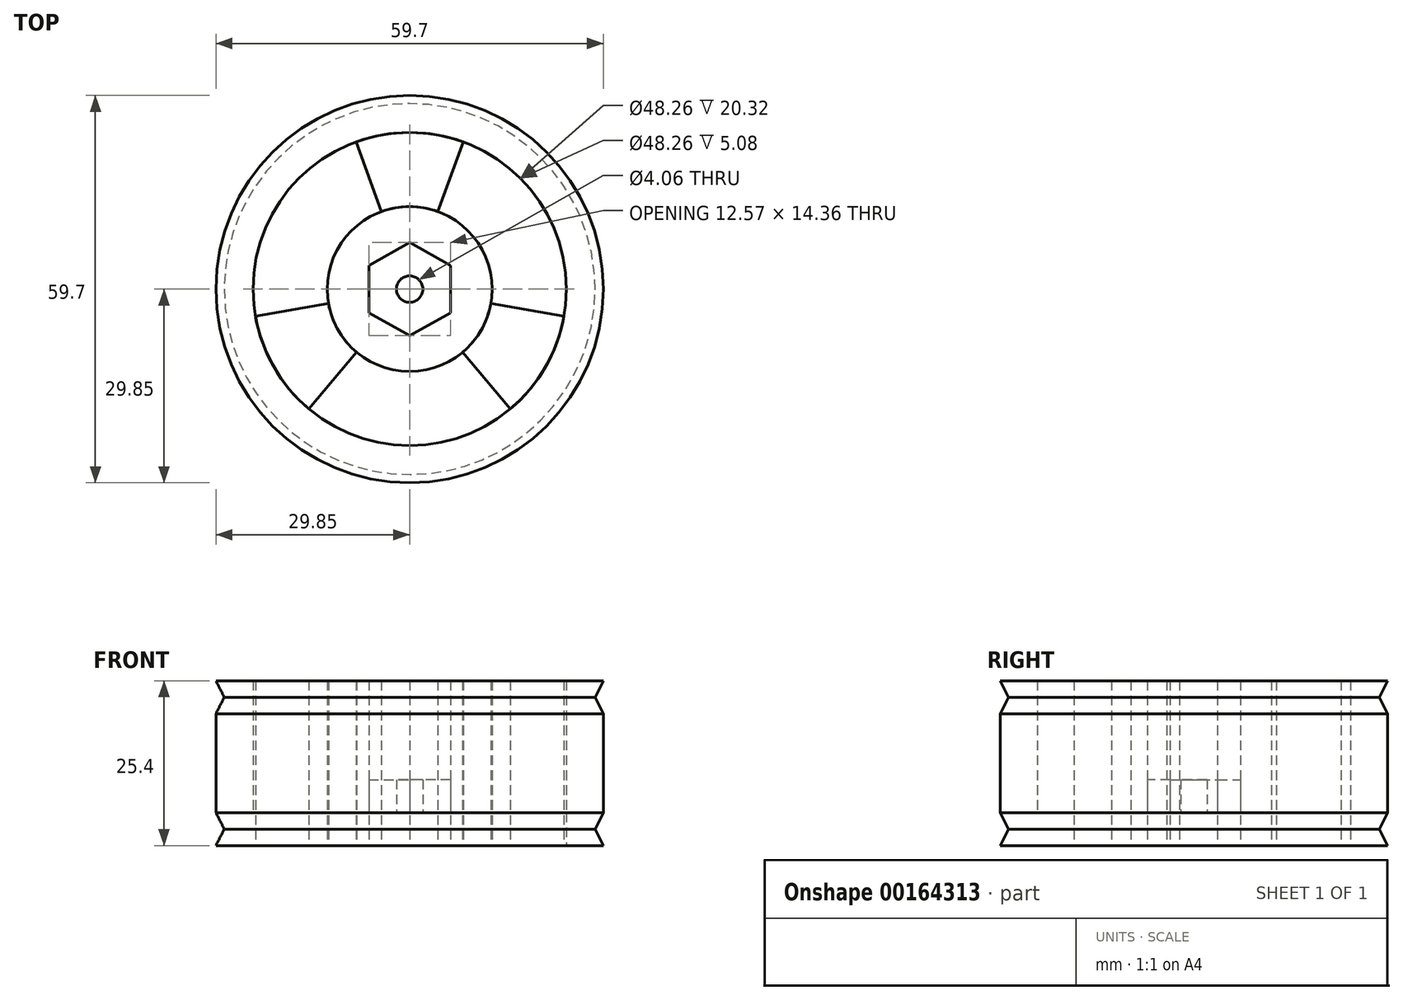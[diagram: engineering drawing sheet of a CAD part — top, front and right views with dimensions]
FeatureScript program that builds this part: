
annotation { "Feature Type Name" : "Feature", "Feature Type Description" : "" }
export const myFeature = defineFeature(function(context is Context, id is Id, definition is map)
    precondition{}
    {
        {
            var Q0;
            Q0=qCreatedBy(makeId("Top.planeOp"),FACE);
            var sketch = newSketch(context, id + "F0", { "sketchPlane" : qUnion([Q0])});
            skCircle(sketch, "E0", {"center": v(0, 0) * mm, "radius": 29.85 * mm});
            skCircle(sketch, "E1", {"center": v(0, 0) * mm, "radius": 28.58 * mm});
            skCircle(sketch, "E2", {"center": v(0, 0) * mm, "radius": 24.13 * mm});
            skCircle(sketch, "E3", {"center": v(0, 0) * mm, "radius": 12.7 * mm});
            skPoint(sketch, "E4.center", {"position": v(-2.54, -2.48) * mm});
            skCircle(sketch, "E5", {"center": v(0, 0) * mm, "radius": 2.03 * mm});
            skLineSegment(sketch, "E6", {"start": v(-4.34, 11.93) * mm, "end": v(-8.25, 22.67) * mm});
            skLineSegment(sketch, "E7", {"start": v(4.34, 11.93) * mm, "end": v(8.25, 22.67) * mm});
            skLineSegment(sketch, "E8.1.0", {"start": v(-8.16, -9.73) * mm, "end": v(-15.51, -18.48) * mm});
            skLineSegment(sketch, "E8.1.1", {"start": v(-12.5, -2.2) * mm, "end": v(-23.76, -4.2) * mm});
            skLineSegment(sketch, "E8.2.0", {"start": v(12.5, -2.2) * mm, "end": v(23.76, -4.2) * mm});
            skLineSegment(sketch, "E8.2.1", {"start": v(8.16, -9.73) * mm, "end": v(15.51, -18.48) * mm});
            skLineSegment(sketch, "E9.0", {"start": v(6.29, 3.64) * mm, "end": v(0, 7.18) * mm});
            skLineSegment(sketch, "E10.0", {"start": v(-6.29, 3.64) * mm, "end": v(0, 7.18) * mm});
            skLineSegment(sketch, "E11.0", {"start": v(-6.29, 0) * mm, "end": v(-6.29, 3.64) * mm});
            skLineSegment(sketch, "E12.0", {"start": v(-6.29, 0) * mm, "end": v(-6.29, -3.65) * mm});
            skLineSegment(sketch, "E13.0", {"start": v(-6.29, -3.65) * mm, "end": v(0, -7.18) * mm});
            skLineSegment(sketch, "E14.0", {"start": v(6.29, -3.65) * mm, "end": v(0, -7.18) * mm});
            skLineSegment(sketch, "E15.0", {"start": v(6.29, 0) * mm, "end": v(6.29, 3.64) * mm});
            skLineSegment(sketch, "E16.0", {"start": v(6.29, 0) * mm, "end": v(6.29, -3.65) * mm});
            skSolve(sketch);
        }
        {
            var Q0;
            Q0=makeQuery(id+"F0.imprint","IMPRINT",FACE,{"disambiguationData":[TD([[makeQuery(id+"F0.imprint","IMPRINT",EDGE,{"derivedFrom":sQuery(id+"F0.wireOp",EDGE,"E0")}),1.0]])]});
            var Q1;
            Q1=makeQuery(id+"F0.imprint","IMPRINT",FACE,{"disambiguationData":[TD([[makeQuery(id+"F0.imprint","IMPRINT",EDGE,{"derivedFrom":sQuery(id+"F0.wireOp",EDGE,"E1")}),1.0]])]});
            var Q2;
            {var subQ0=sQuery(id+"F0.wireOp",EDGE,"GJQjjHoj-4Gza-Cqvl-y5zt-PDY4y1vQ9Ejl");Q2=makeQuery(id+"F0.imprint","IMPRINT",FACE,{"disambiguationData":[TD([[makeQuery(id+"F0.imprint","IMPRINT",EDGE,{"derivedFrom":subQ0}),1.0]])]});}
            var Q3;
            {var subQ0=sQuery(id+"F0.wireOp",EDGE,"5clKBCeK-UdE9-CNba-pvyQ-iNDw4SjmlcOe");Q3=makeQuery(id+"F0.imprint","IMPRINT",FACE,{"disambiguationData":[TD([[makeQuery(id+"F0.imprint","IMPRINT",EDGE,{"derivedFrom":subQ0}),-1.0]])]});}
            var Q4;
            {var subQ0=sQuery(id+"F0.wireOp",EDGE,"E4.8.0");Q4=makeQuery(id+"F0.imprint","IMPRINT",FACE,{"disambiguationData":[TD([[makeQuery(id+"F0.imprint","IMPRINT",EDGE,{"derivedFrom":subQ0}),1.0]])]});}
            var Q5;
            {var subQ0=sQuery(id+"F0.wireOp",EDGE,"E4.7.0");Q5=makeQuery(id+"F0.imprint","IMPRINT",FACE,{"disambiguationData":[TD([[makeQuery(id+"F0.imprint","IMPRINT",EDGE,{"derivedFrom":subQ0}),1.0]])]});}
            var Q6;
            {var subQ0=sQuery(id+"F0.wireOp",EDGE,"E4.6.0");Q6=makeQuery(id+"F0.imprint","IMPRINT",FACE,{"disambiguationData":[TD([[makeQuery(id+"F0.imprint","IMPRINT",EDGE,{"derivedFrom":subQ0}),1.0]])]});}
            var Q7;
            {var subQ0=sQuery(id+"F0.wireOp",EDGE,"E4.5.0");Q7=makeQuery(id+"F0.imprint","IMPRINT",FACE,{"disambiguationData":[TD([[makeQuery(id+"F0.imprint","IMPRINT",EDGE,{"derivedFrom":subQ0}),1.0]])]});}
            var Q8;
            {var subQ0=sQuery(id+"F0.wireOp",EDGE,"E4.4.0");Q8=makeQuery(id+"F0.imprint","IMPRINT",FACE,{"disambiguationData":[TD([[makeQuery(id+"F0.imprint","IMPRINT",EDGE,{"derivedFrom":subQ0}),1.0]])]});}
            var Q9;
            {var subQ0=sQuery(id+"F0.wireOp",EDGE,"E4.3.0");Q9=makeQuery(id+"F0.imprint","IMPRINT",FACE,{"disambiguationData":[TD([[makeQuery(id+"F0.imprint","IMPRINT",EDGE,{"derivedFrom":subQ0}),1.0]])]});}
            var Q10;
            {var subQ0=sQuery(id+"F0.wireOp",EDGE,"E4.2.0");Q10=makeQuery(id+"F0.imprint","IMPRINT",FACE,{"disambiguationData":[TD([[makeQuery(id+"F0.imprint","IMPRINT",EDGE,{"derivedFrom":subQ0}),1.0]])]});}
            var Q11;
            {var subQ0=sQuery(id+"F0.wireOp",EDGE,"E4.1.0");Q11=makeQuery(id+"F0.imprint","IMPRINT",FACE,{"disambiguationData":[TD([[makeQuery(id+"F0.imprint","IMPRINT",EDGE,{"derivedFrom":subQ0}),1.0]])]});}
            extrude(context, id + "F1", {"entities" : qUnion([Q0, Q1, Q2, Q3, Q4, Q5, Q6, Q7, Q8, Q9, Q10, Q11]), "depth" : 5.08 * mm});
        }
        {
            var Q0;
            Q0=qCreatedBy(makeId("Front.planeOp"),FACE);
            var sketch = newSketch(context, id + "F2", { "sketchPlane" : qUnion([Q0])});
            skLineSegment(sketch, "E17.0", {"start": v(-29.85, 5.08) * mm, "end": v(29.85, 5.08) * mm});
            skLineSegment(sketch, "E18.0", {"start": v(-29.85, 0) * mm, "end": v(29.85, 0) * mm});
            skLineSegment(sketch, "E19.0", {"start": v(-28.58, 0) * mm, "end": v(28.58, 0) * mm});
            skLineSegment(sketch, "E20", {"start": v(-29.85, 0) * mm, "end": v(-28.58, 0) * mm});
            skLineSegment(sketch, "E21", {"start": v(-29.85, 5.08) * mm, "end": v(-29.85, 0) * mm});
            skLineSegment(sketch, "E22", {"start": v(0, 0) * mm, "end": v(0, 18.3) * mm});
            skPoint(sketch, "E22.endSnap0", {"position": v(0, 5.08) * mm});
            skLineSegment(sketch, "E23", {"start": v(0, 18.3) * mm, "end": v(0, -17.88) * mm});
            skPoint(sketch, "E23.endSnap0", {"position": v(0, 0) * mm});
            skPoint(sketch, "E24", {"position": v(-28.58, 0) * mm});
            skLineSegment(sketch, "E25", {"start": v(-29.85, 0) * mm, "end": v(-28.58, 2.54) * mm});
            skLineSegment(sketch, "E26", {"start": v(-28.58, 2.54) * mm, "end": v(-29.85, 5.08) * mm});
            skLineSegment(sketch, "E27", {"start": v(-12.7, 25.4) * mm, "end": v(-29.85, 25.4) * mm});
            skLineSegment(sketch, "E28", {"start": v(-29.85, 25.4) * mm, "end": v(-29.85, 20.32) * mm});
            skLineSegment(sketch, "E29", {"start": v(-28.58, 20.32) * mm, "end": v(-28.58, 25.4) * mm});
            skLineSegment(sketch, "E30", {"start": v(-29.85, 20.32) * mm, "end": v(-28.58, 20.32) * mm});
            skLineSegment(sketch, "E31", {"start": v(-29.85, 20.32) * mm, "end": v(-28.58, 22.86) * mm});
            skLineSegment(sketch, "E32", {"start": v(-28.58, 22.86) * mm, "end": v(-29.85, 25.4) * mm});
            skSolve(sketch);
        }
        {
            var Q0;
            Q0=makeQuery(id+"F2.imprint","IMPRINT",FACE,{"disambiguationData":[TD([[makeQuery(id+"F2.imprint","IMPRINT",EDGE,{"derivedFrom":sQuery(id+"F2.wireOp",EDGE,"E21")}),1.0]])]});
            var Q1;
            Q1=makeQuery(id+"F2.imprint","IMPRINT",FACE,{"disambiguationData":[TD([[makeQuery(id+"F2.imprint","IMPRINT",EDGE,{"derivedFrom":sQuery(id+"F2.wireOp",EDGE,"E28")}),1.0]])]});
            var Q2;
            Q2=sQuery(id+"F2.wireOp",EDGE,"E23");
            revolve(context, id + "F3", {"operationType" : NewBodyOperationType.REMOVE, "entities" : qUnion([Q0, Q1]), "axis" : qUnion([Q2]), "revolveType" : RevolveType.FULL, "oppositeDirection" : true});
        }
        {
            var Q0;
            {var subQ0=sQuery(id+"F0.wireOp",EDGE,"E8.1.0");Q0=makeQuery(id+"F0.imprint","IMPRINT",FACE,{"disambiguationData":[TD([[makeQuery(id+"F0.imprint","IMPRINT",EDGE,{"derivedFrom":subQ0}),-1.0]])]});}
            var Q1;
            {var subQ0=sQuery(id+"F0.wireOp",EDGE,"E6");Q1=makeQuery(id+"F0.imprint","IMPRINT",FACE,{"disambiguationData":[TD([[makeQuery(id+"F0.imprint","IMPRINT",EDGE,{"derivedFrom":subQ0}),-1.0]])]});}
            var Q2;
            {var subQ0=sQuery(id+"F0.wireOp",EDGE,"E8.2.0");Q2=makeQuery(id+"F0.imprint","IMPRINT",FACE,{"disambiguationData":[TD([[makeQuery(id+"F0.imprint","IMPRINT",EDGE,{"derivedFrom":subQ0}),-1.0]])]});}
            extrude(context, id + "F4", {"entities" : qUnion([Q0, Q1, Q2]), "depth" : 25.4 * mm});
        }
        {
            var Q0;
            Q0=makeQuery(id+"F1.opExtrude","CAP_FACE",FACE,{"disambiguationData":[OSD([sQuery(id+"F0.wireOp",EDGE,"E0"),sQuery(id+"F0.wireOp",EDGE,"E2")])],"isStart":false});
            var Q1;
            Q1=makeQuery(id+"F4.opExtrude","CAP_FACE",FACE,{"disambiguationData":[OSD([sQuery(id+"F0.wireOp",EDGE,"E2"),sQuery(id+"F0.wireOp",EDGE,"E3"),sQuery(id+"F0.wireOp",EDGE,"E8.1.0"),sQuery(id+"F0.wireOp",EDGE,"E8.1.1")])],"isStart":false});
            extrude(context, id + "F5", {"entities" : qUnion([Q0]), "endBound" : BoundingType.UP_TO_SURFACE, "endBoundEntityFace" : qUnion([Q1]), "depth" : 25.4 * mm});
        }
        {
            var Q0;
            Q0=makeQuery(id+"F2.imprint","IMPRINT",FACE,{"disambiguationData":[TD([[makeQuery(id+"F2.imprint","IMPRINT",EDGE,{"derivedFrom":sQuery(id+"F2.wireOp",EDGE,"E28")}),1.0]])]});
            var Q1;
            Q1=sQuery(id+"F2.wireOp",EDGE,"E23");
            revolve(context, id + "F6", {"operationType" : NewBodyOperationType.REMOVE, "entities" : qUnion([Q0]), "axis" : qUnion([Q1]), "revolveType" : RevolveType.FULL, "oppositeDirection" : true});
        }
        {
            var Q0;
            Q0=makeQuery(id+"F0.imprint","IMPRINT",FACE,{"disambiguationData":[TD([[makeQuery(id+"F0.imprint","IMPRINT",EDGE,{"derivedFrom":sQuery(id+"F0.wireOp",EDGE,"E9.0")}),-1.0]])]});
            extrude(context, id + "F7", {"entities" : qUnion([Q0]), "depth" : 25.4 * mm});
        }
        {
            var Q0;
            Q0=makeQuery(id+"F0.imprint","IMPRINT",FACE,{"disambiguationData":[TD([[makeQuery(id+"F0.imprint","IMPRINT",EDGE,{"derivedFrom":sQuery(id+"F0.wireOp",EDGE,"E5")}),-1.0]])]});
            extrude(context, id + "F8", {"entities" : qUnion([Q0]), "depth" : 5.08 * mm});
        }
        {
            var Q0;
            Q0=makeQuery(id+"F8.opExtrude","SWEPT_BODY",BODY,{"disambiguationData":[OSD([sQuery(id+"F0.wireOp",EDGE,"E5"),sQuery(id+"F0.wireOp",EDGE,"E9.0"),sQuery(id+"F0.wireOp",EDGE,"E10.0"),sQuery(id+"F0.wireOp",EDGE,"E11.0"),sQuery(id+"F0.wireOp",EDGE,"E12.0"),sQuery(id+"F0.wireOp",EDGE,"E13.0"),sQuery(id+"F0.wireOp",EDGE,"E14.0"),sQuery(id+"F0.wireOp",EDGE,"E15.0"),sQuery(id+"F0.wireOp",EDGE,"E16.0")])]});
            var Q1;
            Q1=makeQuery(id+"F7.opExtrude","CAP_FACE",FACE,{"disambiguationData":[OSD([sQuery(id+"F0.wireOp",EDGE,"E3"),sQuery(id+"F0.wireOp",EDGE,"E9.0"),sQuery(id+"F0.wireOp",EDGE,"E10.0"),sQuery(id+"F0.wireOp",EDGE,"E11.0"),sQuery(id+"F0.wireOp",EDGE,"E12.0"),sQuery(id+"F0.wireOp",EDGE,"E13.0"),sQuery(id+"F0.wireOp",EDGE,"E14.0"),sQuery(id+"F0.wireOp",EDGE,"E15.0"),sQuery(id+"F0.wireOp",EDGE,"E16.0")])],"isStart":false});
            transform(context, id + "F9", {"entities" : qUnion([Q0]), "transformType" : TransformType.TRANSLATION_DISTANCE, "transformDirection" : qUnion([Q1]), "distance" : 5.08 * mm, "makeCopy" : false});
        }
    });
